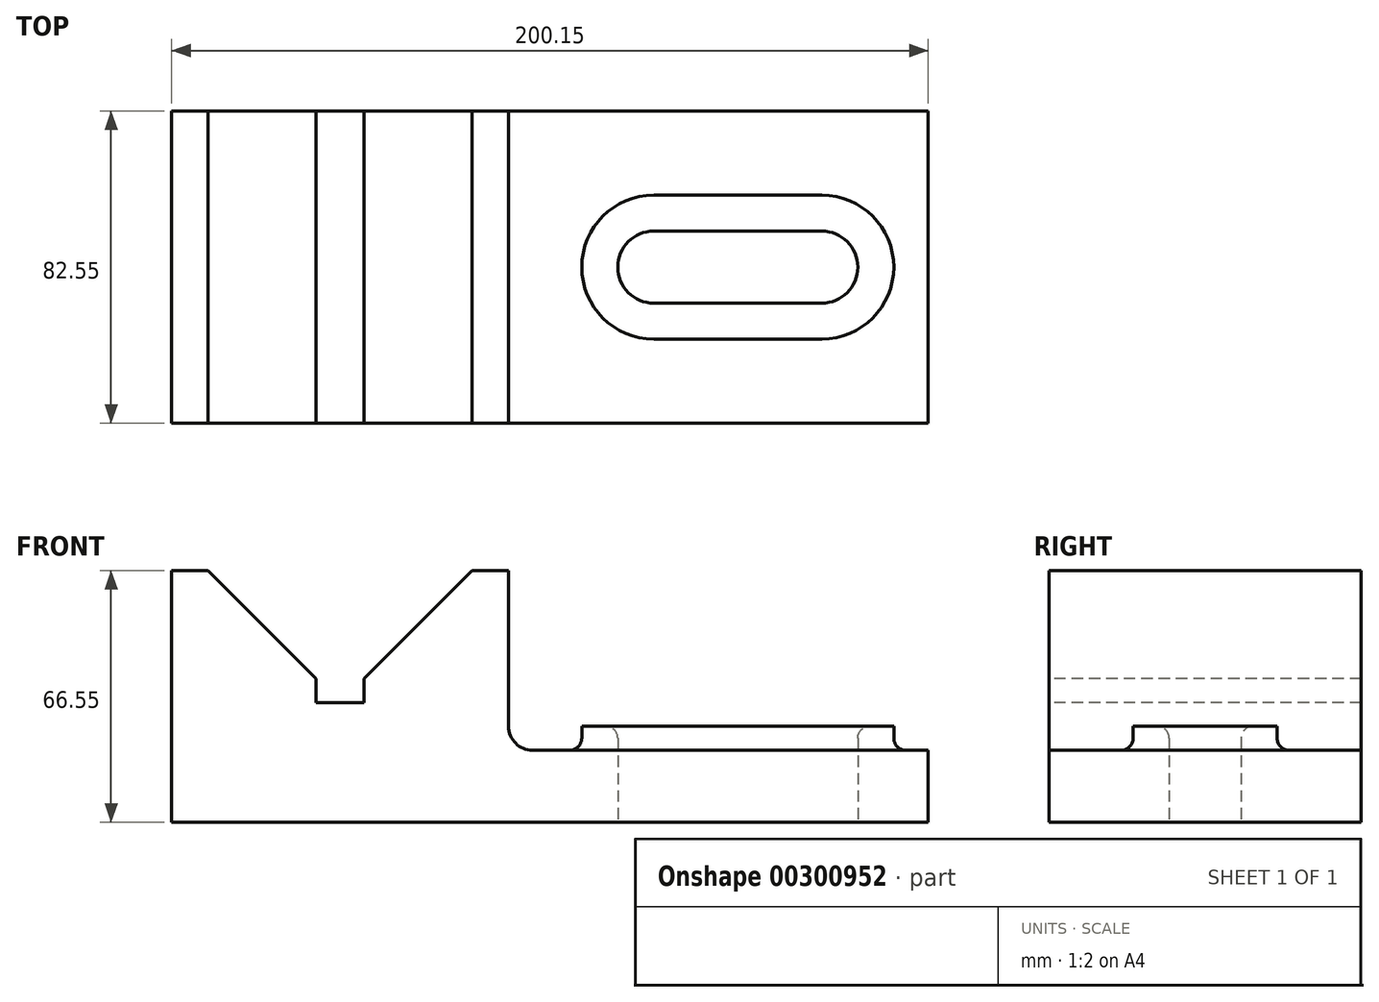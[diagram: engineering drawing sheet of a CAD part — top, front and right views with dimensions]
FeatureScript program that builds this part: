
annotation { "Feature Type Name" : "Feature", "Feature Type Description" : "" }
export const myFeature = defineFeature(function(context is Context, id is Id, definition is map)
    precondition{}
    {
        {
            var Q0;
            Q0=qCreatedBy(makeId("Top.planeOp"),FACE);
            var sketch = newSketch(context, id + "F0", { "sketchPlane" : qUnion([Q0])});
            skLineSegment(sketch, "E0.bottom", {"start": v(-66.37, 21.43) * mm, "end": v(133.78, 21.43) * mm});
            skLineSegment(sketch, "E0.top", {"start": v(-66.37, -61.12) * mm, "end": v(133.78, -61.12) * mm});
            skLineSegment(sketch, "E0.left", {"start": v(-66.37, 21.43) * mm, "end": v(-66.37, -61.12) * mm});
            skLineSegment(sketch, "E0.right", {"start": v(133.78, 21.43) * mm, "end": v(133.78, -61.12) * mm});
            skSolve(sketch);
        }
        {
            var Q0;
            Q0 = qSketchRegion(id + "F0", true);
            extrude(context, id + "F1", {"entities" : qUnion([Q0]), "depth" : 66.55 * mm});
        }
        {
            var Q0;
            Q0=makeQuery(id+"F1.opExtrude","SWEPT_FACE",FACE,{"disambiguationData":[OSD([sQuery(id+"F0.wireOp",EDGE,"E0.top")])]});
            var sketch = newSketch(context, id + "F2", { "sketchPlane" : qUnion([Q0])});
            skLineSegment(sketch, "E1", {"start": v(-66.37, 66.55) * mm, "end": v(-56.72, 66.55) * mm});
            skLineSegment(sketch, "E2", {"start": v(13.13, 66.55) * mm, "end": v(22.78, 66.55) * mm});
            skLineSegment(sketch, "E3", {"start": v(-56.72, 66.55) * mm, "end": v(-28.15, 37.97) * mm});
            skLineSegment(sketch, "E4", {"start": v(-15.45, 37.97) * mm, "end": v(13.13, 66.55) * mm});
            skLineSegment(sketch, "E5.top", {"start": v(-28.15, 31.62) * mm, "end": v(-15.45, 31.62) * mm});
            skLineSegment(sketch, "E5.left", {"start": v(-28.15, 37.97) * mm, "end": v(-28.15, 31.62) * mm});
            skLineSegment(sketch, "E5.right", {"start": v(-15.45, 37.97) * mm, "end": v(-15.45, 31.62) * mm});
            skSolve(sketch);
        }
        {
            var Q0;
            {var subQ1=sQuery(id+"F2.wireOp",EDGE,"E3");Q0=makeQuery(id+"F2.imprint","IMPRINT",FACE,{"disambiguationData":[TD([[makeQuery(id+"F2.imprint","IMPRINT",EDGE,{"derivedFrom":subQ1}),1.0]])]});}
            extrude(context, id + "F3", {"entities" : qUnion([Q0]), "operationType" : NewBodyOperationType.REMOVE, "endBound" : BoundingType.THROUGH_ALL, "oppositeDirection" : true, "depth" : 25.4 * mm});
        }
        {
            var Q0;
            Q0=makeQuery(id+"F1.opExtrude","SWEPT_FACE",FACE,{"disambiguationData":[OSD([sQuery(id+"F0.wireOp",EDGE,"E0.top")])]});
            var sketch = newSketch(context, id + "F4", { "sketchPlane" : qUnion([Q0])});
            skLineSegment(sketch, "E6.bottom", {"start": v(133.78, 19.05) * mm, "end": v(29.13, 19.05) * mm});
            skLineSegment(sketch, "E6.top", {"start": v(133.78, 66.55) * mm, "end": v(22.78, 66.55) * mm});
            skLineSegment(sketch, "E6.left", {"start": v(133.78, 19.05) * mm, "end": v(133.78, 66.55) * mm});
            skLineSegment(sketch, "E6.right", {"start": v(22.78, 25.4) * mm, "end": v(22.78, 66.55) * mm});
            skArc(sketch, "E7", {"start": v(22.78, 25.4) * mm, "mid": v(24.64, 20.9) * mm, "end": v(29.13, 19.05) * mm});
            skSolve(sketch);
        }
        {
            var Q0;
            Q0=makeQuery(id+"F4.imprint","IMPRINT",FACE,{"disambiguationData":[TD([[makeQuery(id+"F4.imprint","IMPRINT",EDGE,{"derivedFrom":sQuery(id+"F4.wireOp",EDGE,"E6.bottom")}),-1.0]])]});
            extrude(context, id + "F5", {"entities" : qUnion([Q0]), "operationType" : NewBodyOperationType.REMOVE, "endBound" : BoundingType.THROUGH_ALL, "oppositeDirection" : true, "depth" : 25.4 * mm});
        }
        {
            var Q0;
            Q0=makeQuery(id+"F5.boolean.opBoolean","COPY",FACE,{"derivedFrom":makeQuery(id+"F5.opExtrude","SWEPT_FACE",FACE,{"disambiguationData":[OSD([sQuery(id+"F4.wireOp",EDGE,"E6.bottom")])]})});
            var sketch = newSketch(context, id + "F6", { "sketchPlane" : qUnion([Q0])});
            skArc(sketch, "E8", {"start": v(105.62, -38.9) * mm, "mid": v(124.67, -19.85) * mm, "end": v(105.62, -0.8) * mm});
            skArc(sketch, "E9", {"start": v(105.62, -29.37) * mm, "mid": v(115.14, -19.85) * mm, "end": v(105.62, -10.32) * mm});
            skArc(sketch, "E10", {"start": v(61.17, -0.8) * mm, "mid": v(42.12, -19.85) * mm, "end": v(61.17, -38.9) * mm});
            skArc(sketch, "E11", {"start": v(61.17, -10.32) * mm, "mid": v(51.64, -19.85) * mm, "end": v(61.17, -29.37) * mm});
            skLineSegment(sketch, "E12", {"start": v(61.17, -10.32) * mm, "end": v(105.62, -10.32) * mm});
            skLineSegment(sketch, "E13", {"start": v(61.17, -29.37) * mm, "end": v(105.62, -29.37) * mm});
            skLineSegment(sketch, "E14", {"start": v(61.17, -0.8) * mm, "end": v(105.62, -0.8) * mm});
            skLineSegment(sketch, "E15", {"start": v(61.17, -38.9) * mm, "end": v(105.62, -38.9) * mm});
            skSolve(sketch);
        }
        {
            var Q0;
            Q0=makeQuery(id+"F6.imprint","IMPRINT",FACE,{"disambiguationData":[TD([[makeQuery(id+"F6.imprint","IMPRINT",EDGE,{"derivedFrom":sQuery(id+"F6.wireOp",EDGE,"E8")}),1.0]])]});
            extrude(context, id + "F7", {"entities" : qUnion([Q0]), "operationType" : NewBodyOperationType.ADD, "depth" : 6.35 * mm});
        }
        {
            var Q0;
            Q0=makeQuery(id+"F7.boolean.opBoolean","SPLIT",FACE,{"disambiguationData":[TD([makeQuery(id+"F7.opExtrude","SWEPT_FACE",FACE,{"disambiguationData":[OSD([sQuery(id+"F6.wireOp",EDGE,"E9")])]})])],"derivedFrom":makeQuery(id+"F5.boolean.opBoolean","COPY",FACE,{"derivedFrom":makeQuery(id+"F5.opExtrude","SWEPT_FACE",FACE,{"disambiguationData":[OSD([sQuery(id+"F4.wireOp",EDGE,"E6.bottom")])]})})});
            extrude(context, id + "F8", {"entities" : qUnion([Q0]), "operationType" : NewBodyOperationType.REMOVE, "endBound" : BoundingType.THROUGH_ALL, "oppositeDirection" : true, "depth" : 25.4 * mm});
        }
        {
            var Q0;
            Q0=makeQuery(id+"F7.opExtrude","CAP_EDGE",EDGE,{"disambiguationData":[OSD([sQuery(id+"F6.wireOp",EDGE,"E15")])],"isStart":true});
            var Q1;
            Q1=makeQuery(id+"F7.opExtrude","CAP_EDGE",EDGE,{"disambiguationData":[OSD([sQuery(id+"F6.wireOp",EDGE,"E10")])],"isStart":true});
            var Q2;
            Q2=makeQuery(id+"F7.opExtrude","CAP_EDGE",EDGE,{"disambiguationData":[OSD([sQuery(id+"F6.wireOp",EDGE,"E8")])],"isStart":true});
            var Q3;
            Q3=makeQuery(id+"F7.opExtrude","CAP_EDGE",EDGE,{"disambiguationData":[OSD([sQuery(id+"F6.wireOp",EDGE,"E12")])],"isStart":false});
            fillet(context, id + "F9", {"entities" : qUnion([Q0, Q1, Q2, Q3]), "radius" : 3.17 * mm, "tangentPropagation" : true, "allowEdgeOverflow" : false});
        }
    });
